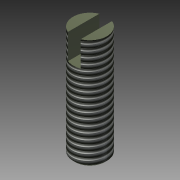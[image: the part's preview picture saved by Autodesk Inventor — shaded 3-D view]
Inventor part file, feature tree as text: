
AUTODESK INVENTOR PART (.ipt)
format: ipt  version: 2015 (Build 190159000, 159)  size: 97,792 bytes
history: native  units: mm
features: extrude x2, sketch x2, thread x1, chamfer x1
ambient origin geometry x8: Origin, YZ Plane, XZ Plane, XY Plane, X Axis, Y Axis, Z Axis, Center Point
bodies: 实体1 (feature_tree)
feature tree (6):
  extrude  "拉伸1"  Depth=13.0mm TaperAngle=0.0deg
  extrude  "拉伸2"  Depth=3.0mm TaperAngle=0.0deg
  thread  "螺纹1"  [1 undecoded]
  chamfer  "倒角1"  Distance=2.0mm Angle=45.0deg
  sketch  "草图1"  dims[d0=4.0mm d1=13.0mm d2=0.0mm]
  sketch  "草图2"  dims[d3=1.5mm d4=3.0mm d5=0.0mm d6=10.0mm d7=0.0mm d8=0.25mm d9=2.0mm d10=45.0deg]
note: 1 required parameter value undecoded (feature->parameter linkage not recoverable at this tier; creation-order binding heuristic only, values carry confidence <= 0.55)
